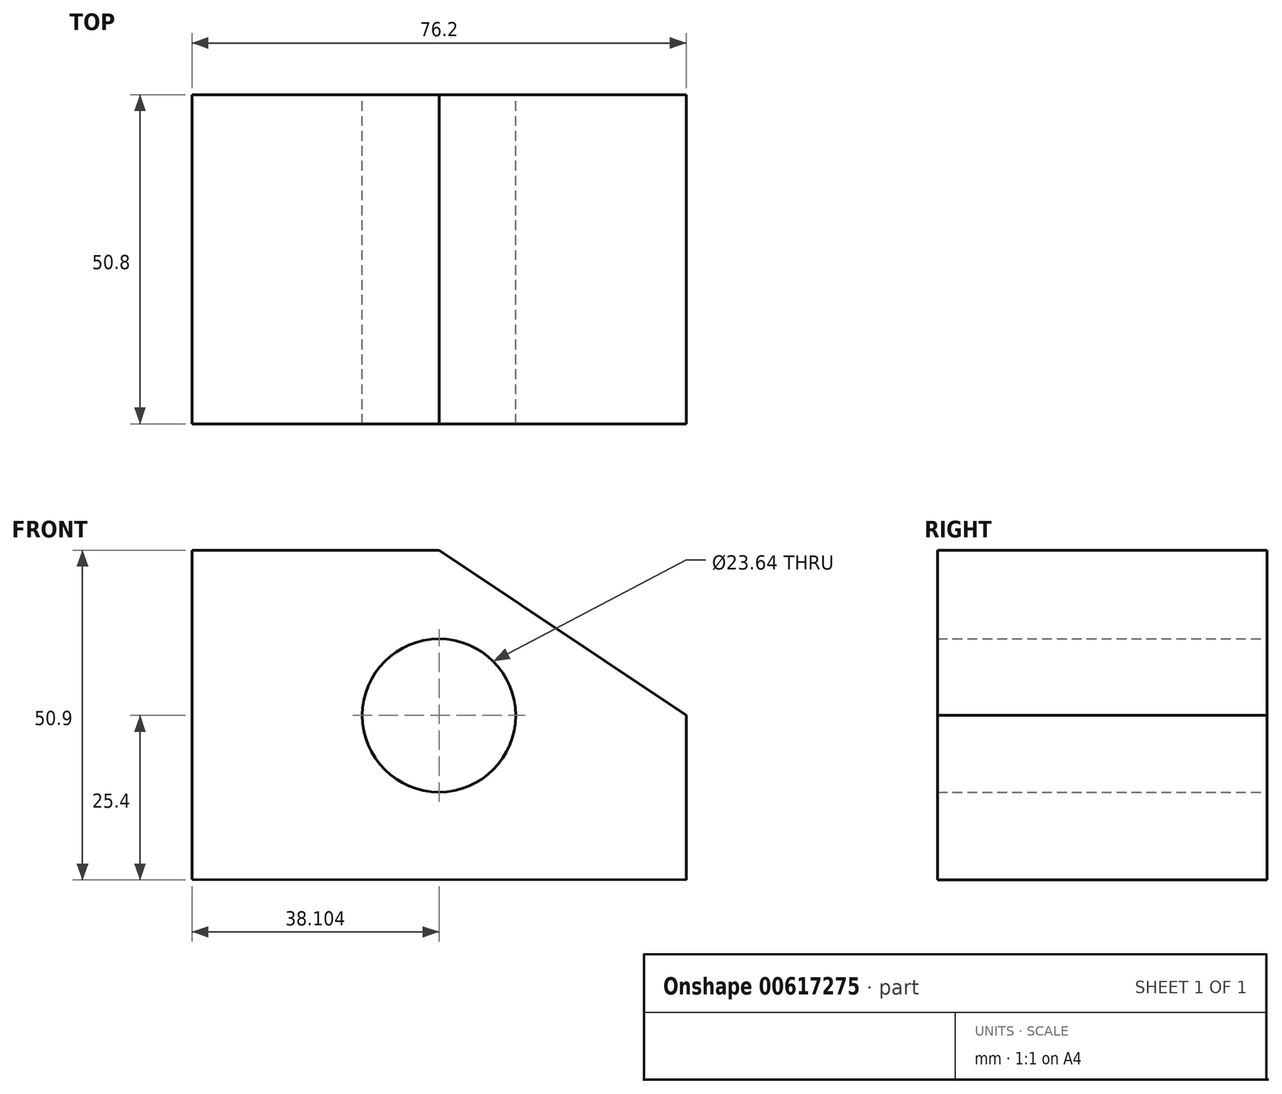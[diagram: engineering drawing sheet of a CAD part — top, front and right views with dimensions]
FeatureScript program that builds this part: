
annotation { "Feature Type Name" : "Feature", "Feature Type Description" : "" }
export const myFeature = defineFeature(function(context is Context, id is Id, definition is map)
    precondition{}
    {
        {
            var Q0;
            Q0=qCreatedBy(makeId("Front.planeOp"),FACE);
            var sketch = newSketch(context, id + "F0", { "sketchPlane" : qUnion([Q0])});
            skLineSegment(sketch, "E0", {"start": v(-51, 25.5) * mm, "end": v(-51, -25.3) * mm});
            skLineSegment(sketch, "E1", {"start": v(-51, 25.5) * mm, "end": v(-12.9, 25.5) * mm});
            skLineSegment(sketch, "E2", {"start": v(-12.9, 25.5) * mm, "end": v(25.2, 0) * mm});
            skLineSegment(sketch, "E3", {"start": v(25.2, 0) * mm, "end": v(25.2, -25.4) * mm});
            skLineSegment(sketch, "E4", {"start": v(-51, -25.3) * mm, "end": v(25.2, -25.4) * mm});
            skCircle(sketch, "E5", {"center": v(-12.9, 0) * mm, "radius": 11.82 * mm});
            skSolve(sketch);
        }
        {
            var Q0;
            Q0=makeQuery(id+"F0.imprint","IMPRINT",FACE,{"disambiguationData":[TD([[makeQuery(id+"F0.imprint","IMPRINT",EDGE,{"derivedFrom":sQuery(id+"F0.wireOp",EDGE,"E0")}),1.0]])]});
            extrude(context, id + "F1", {"entities" : qUnion([Q0]), "depth" : 50.8 * mm, "offsetDistance" : 25.4 * mm});
        }
    });
